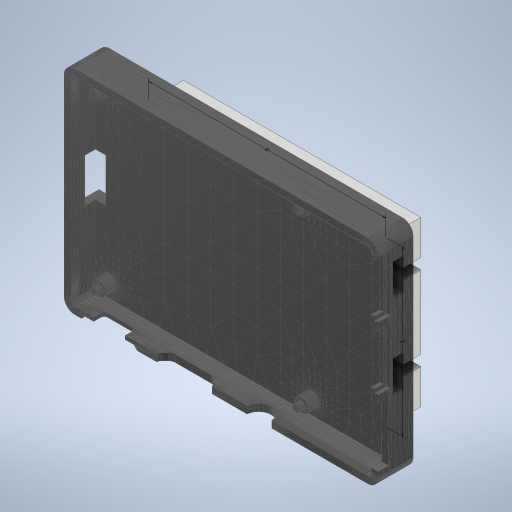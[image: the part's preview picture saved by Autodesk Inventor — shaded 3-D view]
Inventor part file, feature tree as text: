
AUTODESK INVENTOR PART (.ipt)
format: ipt  version: 2023 (Build 270158000, 158)  size: 645,120 bytes
history: native  units: mm
features: sketch x4, extrude x3, other x2
ambient origin geometry x8: Origin, YZ Plane, XZ Plane, XY Plane, X Axis, Y Axis, Z Axis, Center Point
bodies: Solid1 (feature_tree)
feature tree (9):
  other  "bottom"
  sketch  "Sketch1"  dims[d0=68.0mm d1=47.0mm]
  extrude  "Extrusion1"  Depth=47.0mm
  extrude  "Extrusion2"  Depth=10.0mm
  sketch  "Sketch3"  dims[d6=3.0mm d7=3.0mm]
  extrude  "Extrusion3"  Depth=3.0mm
  sketch  "Sketch2"  dims[d2=10.0mm d3=0.0mm d4=10.0mm]
  sketch  "Sketch4"  dims[d8=3.0mm d9=3.0mm d10=6.0mm d11=10.0mm d12=5.0mm d13=3.0mm d14=3.0mm d15=9.0mm d16=3.0mm d17=3.0mm d18=5.0mm d19=68.0mm d20=0.0mm d21=10.0mm d22=5.0mm d23=3.0mm d24=3.0mm d25=9.0mm d26=3.0mm d27=3.0mm d28=68.0mm d29=0.0mm]
  other  "MeshFeature1"
